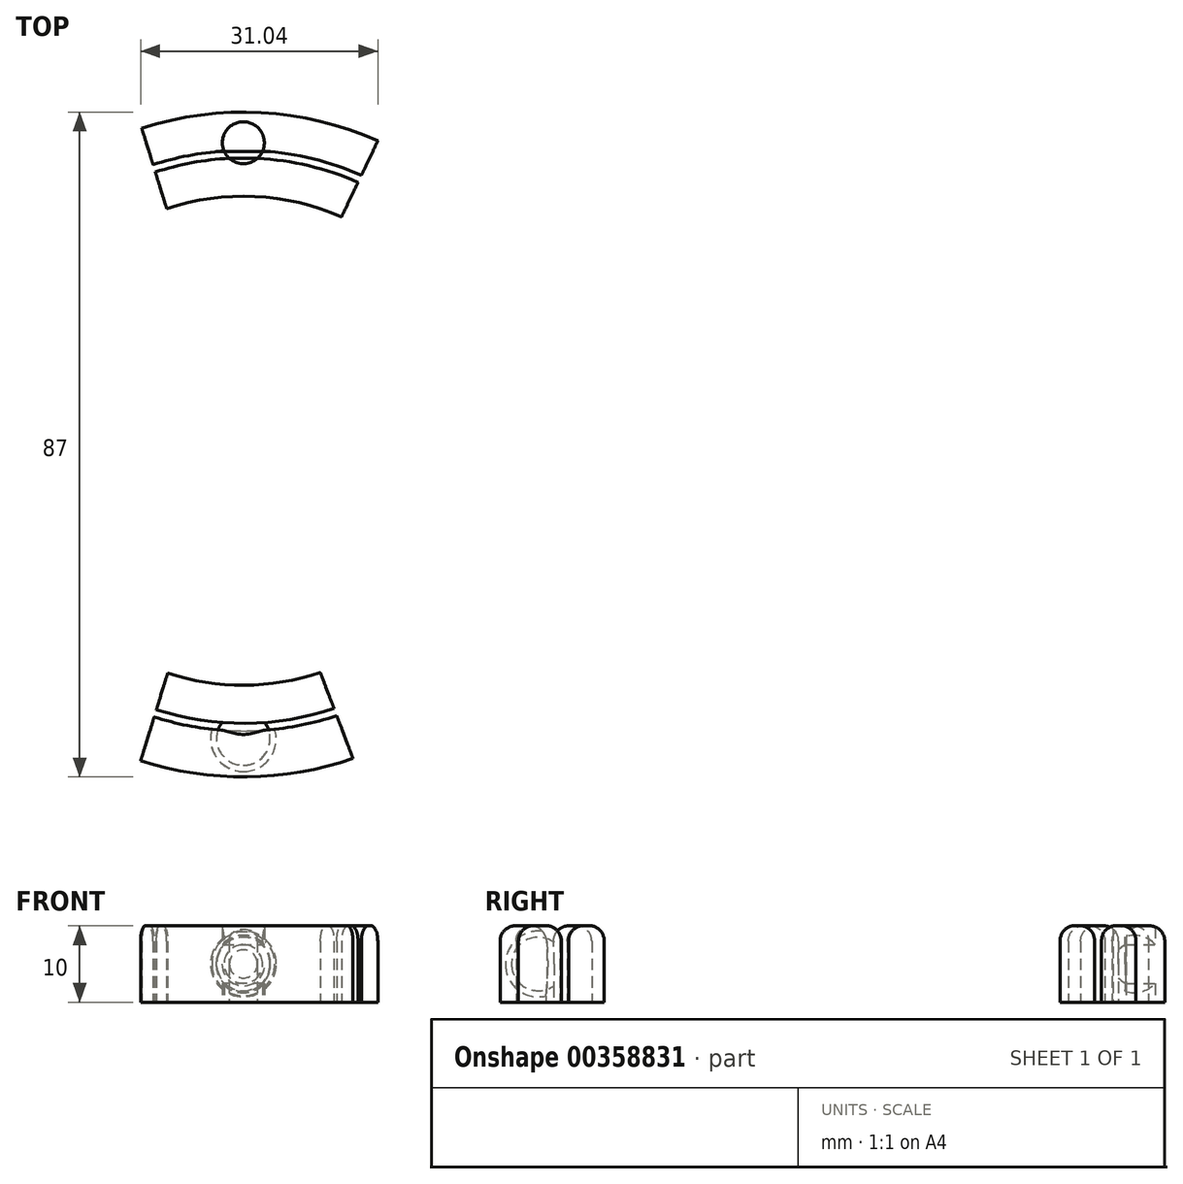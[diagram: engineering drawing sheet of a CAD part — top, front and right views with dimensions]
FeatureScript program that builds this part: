
annotation { "Feature Type Name" : "Feature", "Feature Type Description" : "" }
export const myFeature = defineFeature(function(context is Context, id is Id, definition is map)
    precondition{}
    {
        {
            var Q0;
            Q0=qCreatedBy(makeId("Top.planeOp"),FACE);
            var sketch = newSketch(context, id + "F0", { "sketchPlane" : qUnion([Q0])});
            skArc(sketch, "E0", {"start": v(12.86, 29.3) * mm, "mid": v(1.51, 31.96) * mm, "end": v(-10.03, 30.39) * mm});
            skArc(sketch, "E1.0", {"start": v(15.01, 33.82) * mm, "mid": v(8.57, 36) * mm, "end": v(1.84, 36.95) * mm});
            skArc(sketch, "E2.0", {"start": v(15.44, 34.72) * mm, "mid": v(9.13, 36.89) * mm, "end": v(2.53, 37.92) * mm});
            skArc(sketch, "E3.0", {"start": v(17.6, 39.23) * mm, "mid": v(2.3, 42.94) * mm, "end": v(-13.3, 40.9) * mm});
            skLineSegment(sketch, "E4", {"start": v(-13.3, 40.9) * mm, "end": v(-10.03, 30.39) * mm});
            skLineSegment(sketch, "E5", {"start": v(12.86, 29.3) * mm, "end": v(17.6, 39.23) * mm});
            skCircle(sketch, "E6", {"center": v(0, 39) * mm, "radius": 2.75 * mm});
            skArc(sketch, "E7.0", {"start": v(3.56, 37.83) * mm, "mid": v(0, 42.75) * mm, "end": v(-3.56, 37.83) * mm});
            skArc(sketch, "E8.trimOffspring", {"start": v(-1.84, 36.95) * mm, "mid": v(-6.74, 36.38) * mm, "end": v(-11.52, 35.16) * mm});
            skArc(sketch, "E9.trimOffspring", {"start": v(-2.53, 37.92) * mm, "mid": v(-7.23, 37.3) * mm, "end": v(-11.81, 36.12) * mm});
            skLineSegment(sketch, "E10", {"start": v(0, 43.86) * mm, "end": v(0, 33.98) * mm});
            skLineSegment(sketch, "E11", {"start": v(-1.84, 36.95) * mm, "end": v(1.84, 36.95) * mm});
            skLineSegment(sketch, "E12", {"start": v(-2.53, 37.92) * mm, "end": v(2.53, 37.92) * mm});
            skSolve(sketch);
        }
        {
            var Q0;
            {var subQ3=sQuery(id+"F0.wireOp",EDGE,"E4");var subQ7=sQuery(id+"F0.wireOp",EDGE,"E3.0");var subQ8=makeQuery(id+"F0.imprint","INTERSECT",VERTEX,{"derivedFrom":[subQ7,subQ3]});Q0=makeQuery(id+"F0.imprint","IMPRINT",FACE,{"disambiguationData":[TD([[makeQuery(id+"F0.imprint","IMPRINT",EDGE,{"disambiguationData":[TD([[subQ8,1.0]])],"derivedFrom":subQ7}),1.0]])]});}
            var Q1;
            {var subQ1=sQuery(id+"F0.wireOp",EDGE,"E2.0");var subQ5=sQuery(id+"F0.wireOp",EDGE,"E5");var subQ6=makeQuery(id+"F0.imprint","INTERSECT",VERTEX,{"derivedFrom":[subQ1,subQ5]});Q1=makeQuery(id+"F0.imprint","IMPRINT",FACE,{"disambiguationData":[TD([[makeQuery(id+"F0.imprint","IMPRINT",EDGE,{"disambiguationData":[TD([[subQ6,-1.0]])],"derivedFrom":subQ1}),-1.0]])]});}
            var Q2;
            {var subQ1=sQuery(id+"F0.wireOp",EDGE,"E6");var subQ3=sQuery(id+"F0.wireOp",EDGE,"E10");var subQ4=makeQuery(id+"F0.imprint","INTERSECT",VERTEX,{"disambiguationData":[OD(1.0)],"derivedFrom":[subQ1,subQ3]});Q2=makeQuery(id+"F0.imprint","IMPRINT",FACE,{"disambiguationData":[TD([[makeQuery(id+"F0.imprint","IMPRINT",EDGE,{"disambiguationData":[TD([[subQ4,-1.0]])],"derivedFrom":subQ3}),1.0]])]});}
            var Q3;
            {var subQ1=sQuery(id+"F0.wireOp",EDGE,"E6");var subQ3=sQuery(id+"F0.wireOp",EDGE,"E10");var subQ4=makeQuery(id+"F0.imprint","INTERSECT",VERTEX,{"disambiguationData":[OD(1.0)],"derivedFrom":[subQ1,subQ3]});Q3=makeQuery(id+"F0.imprint","IMPRINT",FACE,{"disambiguationData":[TD([[makeQuery(id+"F0.imprint","IMPRINT",EDGE,{"disambiguationData":[TD([[subQ4,-1.0]])],"derivedFrom":subQ3}),-1.0]])]});}
            var Q4;
            {var subQ0=sQuery(id+"F0.wireOp",EDGE,"E9.trimOffspring");var subQ5=sQuery(id+"F0.wireOp",EDGE,"E7.0");var subQ6=makeQuery(id+"F0.imprint","INTERSECT",VERTEX,{"derivedFrom":[subQ5,subQ0]});Q4=makeQuery(id+"F0.imprint","IMPRINT",FACE,{"disambiguationData":[TD([[makeQuery(id+"F0.imprint","IMPRINT",EDGE,{"disambiguationData":[TD([[subQ6,1.0]])],"derivedFrom":subQ5}),1.0]])]});}
            var Q5;
            {var subQ1=sQuery(id+"F0.wireOp",EDGE,"E2.0");var subQ3=sQuery(id+"F0.wireOp",EDGE,"E7.0");var subQ4=makeQuery(id+"F0.imprint","INTERSECT",VERTEX,{"derivedFrom":[subQ1,subQ3]});Q5=makeQuery(id+"F0.imprint","IMPRINT",FACE,{"disambiguationData":[TD([[makeQuery(id+"F0.imprint","IMPRINT",EDGE,{"disambiguationData":[TD([[subQ4,-1.0]])],"derivedFrom":subQ3}),1.0]])]});}
            extrude(context, id + "F1", {"entities" : qUnion([Q0, Q1, Q2, Q3, Q4, Q5]), "endBound" : BoundingType.SYMMETRIC, "depth" : 10 * mm});
        }
        {
            var Q0;
            Q0=qCreatedBy(makeId("Top.planeOp"),FACE);
            var sketch = newSketch(context, id + "F2", { "sketchPlane" : qUnion([Q0])});
            skArc(sketch, "E13", {"start": v(-9.9, -30.43) * mm, "mid": v(0.1, -32) * mm, "end": v(10.09, -30.37) * mm});
            skArc(sketch, "E14.0", {"start": v(-11.38, -35.2) * mm, "mid": v(0.26, -37) * mm, "end": v(11.87, -35.05) * mm});
            skArc(sketch, "E15.0", {"start": v(-11.67, -36.16) * mm, "mid": v(0.29, -38) * mm, "end": v(12.22, -35.98) * mm});
            skArc(sketch, "E16.0", {"start": v(-13.44, -41.9) * mm, "mid": v(0.48, -44) * mm, "end": v(14.35, -41.6) * mm});
            skCircle(sketch, "E17", {"center": v(0, -39) * mm, "radius": 3.5 * mm});
            skArc(sketch, "E18.0", {"start": v(-4.12, -37.78) * mm, "mid": v(0, -43.3) * mm, "end": v(4.12, -37.78) * mm});
            skLineSegment(sketch, "E19", {"start": v(-9.9, -30.43) * mm, "end": v(-13.44, -41.9) * mm});
            skLineSegment(sketch, "E20", {"start": v(10.09, -30.37) * mm, "end": v(14.35, -41.6) * mm});
            skLineSegment(sketch, "E21", {"start": v(0, -33.12) * mm, "end": v(0, -46.67) * mm});
            skSolve(sketch);
        }
        {
            var Q0;
            {var subQ1=sQuery(id+"F0.wireOp",EDGE,"E0");Q0=makeQuery(id+"F0.imprint","IMPRINT",FACE,{"disambiguationData":[TD([[makeQuery(id+"F0.imprint","IMPRINT",EDGE,{"derivedFrom":subQ1}),-1.0]])]});}
            var Q1;
            {var subQ1=sQuery(id+"F0.wireOp",EDGE,"E6");var subQ3=sQuery(id+"F0.wireOp",EDGE,"E10");var subQ4=makeQuery(id+"F0.imprint","INTERSECT",VERTEX,{"disambiguationData":[OD(0.0)],"derivedFrom":[subQ1,subQ3]});Q1=makeQuery(id+"F0.imprint","IMPRINT",FACE,{"disambiguationData":[TD([[makeQuery(id+"F0.imprint","IMPRINT",EDGE,{"disambiguationData":[TD([[subQ4,1.0]])],"derivedFrom":subQ3}),-1.0]])]});}
            var Q2;
            {var subQ1=sQuery(id+"F0.wireOp",EDGE,"E6");var subQ3=sQuery(id+"F0.wireOp",EDGE,"E10");var subQ4=makeQuery(id+"F0.imprint","INTERSECT",VERTEX,{"disambiguationData":[OD(0.0)],"derivedFrom":[subQ1,subQ3]});Q2=makeQuery(id+"F0.imprint","IMPRINT",FACE,{"disambiguationData":[TD([[makeQuery(id+"F0.imprint","IMPRINT",EDGE,{"disambiguationData":[TD([[subQ4,1.0]])],"derivedFrom":subQ3}),1.0]])]});}
            extrude(context, id + "F3", {"entities" : qUnion([Q0, Q1, Q2]), "endBound" : BoundingType.SYMMETRIC, "depth" : 10 * mm});
        }
        {
            var Q0;
            {var subQ0=sQuery(id+"F0.wireOp",EDGE,"E6");var subQ1=makeQuery(id+"F0.imprint","INTERSECT",VERTEX,{"derivedFrom":[subQ0,sQuery(id+"F0.wireOp",EDGE,"E9.trimOffspring")]});Q0=makeQuery(id+"F0.imprint","IMPRINT",FACE,{"disambiguationData":[TD([[makeQuery(id+"F0.imprint","IMPRINT",EDGE,{"disambiguationData":[TD([[subQ1,1.0]])],"derivedFrom":subQ0}),1.0]])]});}
            var Q1;
            Q1=sQuery(id+"F0.wireOp",EDGE,"E10");
            revolve(context, id + "F4", {"entities" : qUnion([Q0]), "axis" : qUnion([Q1]), "revolveType" : RevolveType.FULL});
        }
        {
            var Q0;
            {var subQ1=sQuery(id+"F0.wireOp",EDGE,"E6");var subQ3=sQuery(id+"F0.wireOp",EDGE,"E10");var subQ4=makeQuery(id+"F0.imprint","INTERSECT",VERTEX,{"disambiguationData":[OD(0.0)],"derivedFrom":[subQ1,subQ3]});Q0=makeQuery(id+"F0.imprint","IMPRINT",FACE,{"disambiguationData":[TD([[makeQuery(id+"F0.imprint","IMPRINT",EDGE,{"disambiguationData":[TD([[subQ4,1.0]])],"derivedFrom":subQ3}),-1.0]])]});}
            var Q1;
            Q1=sQuery(id+"F0.wireOp",EDGE,"E10");
            revolve(context, id + "F5", {"operationType" : NewBodyOperationType.ADD, "entities" : qUnion([Q0]), "axis" : qUnion([Q1]), "revolveType" : RevolveType.FULL});
        }
        {
            var Q0;
            {var subQ0=sQuery(id+"F0.wireOp",EDGE,"E9.trimOffspring");var subQ5=sQuery(id+"F0.wireOp",EDGE,"E7.0");var subQ6=makeQuery(id+"F0.imprint","INTERSECT",VERTEX,{"derivedFrom":[subQ5,subQ0]});Q0=makeQuery(id+"F0.imprint","IMPRINT",FACE,{"disambiguationData":[TD([[makeQuery(id+"F0.imprint","IMPRINT",EDGE,{"disambiguationData":[TD([[subQ6,1.0]])],"derivedFrom":subQ5}),1.0]])]});}
            var Q1;
            Q1=sQuery(id+"F0.wireOp",EDGE,"E10");
            revolve(context, id + "F6", {"operationType" : NewBodyOperationType.REMOVE, "entities" : qUnion([Q0]), "axis" : qUnion([Q1]), "revolveType" : RevolveType.FULL});
        }
        {
            var Q0;
            {var subQ3=sQuery(id+"F0.wireOp",EDGE,"E12");var subQ5=sQuery(id+"F0.wireOp",EDGE,"E10");var subQ7=makeQuery(id+"F0.imprint","INTERSECT",VERTEX,{"derivedFrom":[subQ5,subQ3]});Q0=makeQuery(id+"F0.imprint","IMPRINT",FACE,{"disambiguationData":[TD([[makeQuery(id+"F0.imprint","IMPRINT",EDGE,{"disambiguationData":[TD([[subQ7,-1.0]])],"derivedFrom":subQ5}),-1.0]])]});}
            var Q1;
            Q1=sQuery(id+"F0.wireOp",EDGE,"E10");
            revolve(context, id + "F7", {"operationType" : NewBodyOperationType.ADD, "entities" : qUnion([Q0]), "axis" : qUnion([Q1]), "revolveType" : RevolveType.FULL});
        }
        {
            var Q0;
            {var subQ1=sQuery(id+"F0.wireOp",EDGE,"E6");var subQ3=sQuery(id+"F0.wireOp",EDGE,"E10");var subQ4=makeQuery(id+"F0.imprint","INTERSECT",VERTEX,{"disambiguationData":[OD(0.0)],"derivedFrom":[subQ1,subQ3]});Q0=makeQuery(id+"F0.imprint","IMPRINT",FACE,{"disambiguationData":[TD([[makeQuery(id+"F0.imprint","IMPRINT",EDGE,{"disambiguationData":[TD([[subQ4,1.0]])],"derivedFrom":subQ3}),-1.0]])]});}
            var Q1;
            Q1=sQuery(id+"F0.wireOp",EDGE,"E10");
            revolve(context, id + "F8", {"operationType" : NewBodyOperationType.ADD, "entities" : qUnion([Q0]), "axis" : qUnion([Q1]), "revolveType" : RevolveType.FULL});
        }
        {
            var Q0;
            Q0=makeQuery(id+"F1.opExtrude","CAP_EDGE",EDGE,{"disambiguationData":[OSD([sQuery(id+"F0.wireOp",EDGE,"E3.0")])],"isStart":false});
            var Q1;
            Q1=makeQuery(id+"F1.opExtrude","CAP_EDGE",EDGE,{"disambiguationData":[OSD([sQuery(id+"F0.wireOp",EDGE,"E9.trimOffspring")])],"isStart":false});
            var Q2;
            Q2=makeQuery(id+"F1.opExtrude","CAP_EDGE",EDGE,{"disambiguationData":[OSD([sQuery(id+"F0.wireOp",EDGE,"E12")])],"isStart":false});
            var Q3;
            Q3=makeQuery(id+"F1.opExtrude","CAP_EDGE",EDGE,{"disambiguationData":[OSD([sQuery(id+"F0.wireOp",EDGE,"E2.0")])],"isStart":false});
            var Q4;
            Q4=makeQuery(id+"F3.opExtrude","CAP_EDGE",EDGE,{"disambiguationData":[OSD([sQuery(id+"F0.wireOp",EDGE,"E11")])],"isStart":false});
            var Q5;
            Q5=makeQuery(id+"F3.opExtrude","CAP_EDGE",EDGE,{"disambiguationData":[OSD([sQuery(id+"F0.wireOp",EDGE,"E8.trimOffspring")])],"isStart":false});
            var Q6;
            Q6=makeQuery(id+"F3.opExtrude","CAP_EDGE",EDGE,{"disambiguationData":[OSD([sQuery(id+"F0.wireOp",EDGE,"E1.0")])],"isStart":false});
            var Q7;
            Q7=makeQuery(id+"F3.opExtrude","CAP_EDGE",EDGE,{"disambiguationData":[OSD([sQuery(id+"F0.wireOp",EDGE,"E0")])],"isStart":false});
            fillet(context, id + "F9", {"entities" : qUnion([Q0, Q1, Q2, Q3, Q4, Q5, Q6, Q7]), "radius" : 2 * mm, "tangentPropagation" : true, "allowEdgeOverflow" : false});
        }
        {
            var Q0;
            {var subQ0=sQuery(id+"F2.wireOp",EDGE,"E17");var subQ1=sQuery(id+"F2.wireOp",EDGE,"E14.0");var subQ2=makeQuery(id+"F2.imprint","INTERSECT",VERTEX,{"disambiguationData":[OD(0.0)],"derivedFrom":[subQ1,subQ0]});Q0=makeQuery(id+"F2.imprint","IMPRINT",FACE,{"disambiguationData":[TD([[makeQuery(id+"F2.imprint","IMPRINT",EDGE,{"disambiguationData":[TD([[subQ2,-1.0]])],"derivedFrom":subQ1}),1.0]])]});}
            var Q1;
            {var subQ0=sQuery(id+"F2.wireOp",EDGE,"E17");var subQ1=sQuery(id+"F2.wireOp",EDGE,"E14.0");var subQ2=makeQuery(id+"F2.imprint","INTERSECT",VERTEX,{"disambiguationData":[OD(0.0)],"derivedFrom":[subQ1,subQ0]});Q1=makeQuery(id+"F2.imprint","IMPRINT",FACE,{"disambiguationData":[TD([[makeQuery(id+"F2.imprint","IMPRINT",EDGE,{"disambiguationData":[TD([[subQ2,-1.0]])],"derivedFrom":subQ1}),-1.0]])]});}
            var Q2;
            {var subQ0=sQuery(id+"F2.wireOp",EDGE,"E17");var subQ1=sQuery(id+"F2.wireOp",EDGE,"E15.0");var subQ2=makeQuery(id+"F2.imprint","INTERSECT",VERTEX,{"disambiguationData":[OD(0.0)],"derivedFrom":[subQ1,subQ0]});Q2=makeQuery(id+"F2.imprint","IMPRINT",FACE,{"disambiguationData":[TD([[makeQuery(id+"F2.imprint","IMPRINT",EDGE,{"disambiguationData":[TD([[subQ2,-1.0]])],"derivedFrom":subQ1}),-1.0]])]});}
            var Q3;
            Q3=sQuery(id+"F2.wireOp",EDGE,"E21");
            revolve(context, id + "F10", {"operationType" : NewBodyOperationType.ADD, "entities" : qUnion([Q0, Q1, Q2]), "axis" : qUnion([Q3]), "revolveType" : RevolveType.FULL});
        }
        {
            var Q0;
            {var subQ0=sQuery(id+"F2.wireOp",EDGE,"E18.0");var subQ1=sQuery(id+"F2.wireOp",EDGE,"E15.0");var subQ2=makeQuery(id+"F2.imprint","INTERSECT",VERTEX,{"disambiguationData":[OD(0.0)],"derivedFrom":[subQ1,subQ0]});Q0=makeQuery(id+"F2.imprint","IMPRINT",FACE,{"disambiguationData":[TD([[makeQuery(id+"F2.imprint","IMPRINT",EDGE,{"disambiguationData":[TD([[subQ2,-1.0]])],"derivedFrom":subQ1}),-1.0]])]});}
            var Q1;
            Q1=sQuery(id+"F2.wireOp",EDGE,"E21");
            revolve(context, id + "F11", {"operationType" : NewBodyOperationType.REMOVE, "entities" : qUnion([Q0]), "axis" : qUnion([Q1]), "revolveType" : RevolveType.FULL, "oppositeDirection" : true});
        }
        {
            var Q0;
            {var subQ0=sQuery(id+"F2.wireOp",EDGE,"E17");var subQ1=sQuery(id+"F2.wireOp",EDGE,"E14.0");var subQ2=makeQuery(id+"F2.imprint","INTERSECT",VERTEX,{"disambiguationData":[OD(0.0)],"derivedFrom":[subQ1,subQ0]});Q0=makeQuery(id+"F2.imprint","IMPRINT",FACE,{"disambiguationData":[TD([[makeQuery(id+"F2.imprint","IMPRINT",EDGE,{"disambiguationData":[TD([[subQ2,-1.0]])],"derivedFrom":subQ1}),1.0]])]});}
            var Q1;
            {var subQ0=sQuery(id+"F2.wireOp",EDGE,"E21");var subQ1=sQuery(id+"F2.wireOp",EDGE,"E14.0");var subQ2=makeQuery(id+"F2.imprint","INTERSECT",VERTEX,{"derivedFrom":[subQ1,subQ0]});Q1=makeQuery(id+"F2.imprint","IMPRINT",FACE,{"disambiguationData":[TD([[makeQuery(id+"F2.imprint","IMPRINT",EDGE,{"disambiguationData":[TD([[subQ2,-1.0]])],"derivedFrom":subQ1}),1.0]])]});}
            var Q2;
            {var subQ9=sQuery(id+"F2.wireOp",EDGE,"E13");Q2=makeQuery(id+"F2.imprint","IMPRINT",FACE,{"disambiguationData":[TD([[makeQuery(id+"F2.imprint","IMPRINT",EDGE,{"derivedFrom":subQ9}),-1.0]])]});}
            var Q3;
            {var subQ0=sQuery(id+"F2.wireOp",EDGE,"E17");var subQ1=sQuery(id+"F2.wireOp",EDGE,"E15.0");var subQ2=makeQuery(id+"F2.imprint","INTERSECT",VERTEX,{"disambiguationData":[OD(0.0)],"derivedFrom":[subQ1,subQ0]});Q3=makeQuery(id+"F2.imprint","IMPRINT",FACE,{"disambiguationData":[TD([[makeQuery(id+"F2.imprint","IMPRINT",EDGE,{"disambiguationData":[TD([[subQ2,-1.0]])],"derivedFrom":subQ1}),-1.0]])]});}
            var Q4;
            {var subQ0=sQuery(id+"F2.wireOp",EDGE,"E18.0");var subQ1=sQuery(id+"F2.wireOp",EDGE,"E15.0");var subQ2=makeQuery(id+"F2.imprint","INTERSECT",VERTEX,{"disambiguationData":[OD(0.0)],"derivedFrom":[subQ1,subQ0]});Q4=makeQuery(id+"F2.imprint","IMPRINT",FACE,{"disambiguationData":[TD([[makeQuery(id+"F2.imprint","IMPRINT",EDGE,{"disambiguationData":[TD([[subQ2,-1.0]])],"derivedFrom":subQ1}),-1.0]])]});}
            var Q5;
            {var subQ0=sQuery(id+"F2.wireOp",EDGE,"E19");var subQ1=sQuery(id+"F2.wireOp",EDGE,"E15.0");var subQ2=makeQuery(id+"F2.imprint","INTERSECT",VERTEX,{"derivedFrom":[subQ1,subQ0]});Q5=makeQuery(id+"F2.imprint","IMPRINT",FACE,{"disambiguationData":[TD([[makeQuery(id+"F2.imprint","IMPRINT",EDGE,{"disambiguationData":[TD([[subQ2,-1.0]])],"derivedFrom":subQ1}),-1.0]])]});}
            var Q6;
            {var subQ0=sQuery(id+"F2.wireOp",EDGE,"E18.0");var subQ1=sQuery(id+"F2.wireOp",EDGE,"E15.0");var subQ2=makeQuery(id+"F2.imprint","INTERSECT",VERTEX,{"disambiguationData":[OD(1.0)],"derivedFrom":[subQ1,subQ0]});Q6=makeQuery(id+"F2.imprint","IMPRINT",FACE,{"disambiguationData":[TD([[makeQuery(id+"F2.imprint","IMPRINT",EDGE,{"disambiguationData":[TD([[subQ2,1.0]])],"derivedFrom":subQ1}),-1.0]])]});}
            var Q7;
            {var subQ0=sQuery(id+"F2.wireOp",EDGE,"E20");var subQ1=sQuery(id+"F2.wireOp",EDGE,"E15.0");var subQ2=makeQuery(id+"F2.imprint","INTERSECT",VERTEX,{"derivedFrom":[subQ1,subQ0]});Q7=makeQuery(id+"F2.imprint","IMPRINT",FACE,{"disambiguationData":[TD([[makeQuery(id+"F2.imprint","IMPRINT",EDGE,{"disambiguationData":[TD([[subQ2,1.0]])],"derivedFrom":subQ1}),-1.0]])]});}
            var Q8;
            {var subQ0=sQuery(id+"F2.wireOp",EDGE,"E21");var subQ1=sQuery(id+"F2.wireOp",EDGE,"E15.0");var subQ2=makeQuery(id+"F2.imprint","INTERSECT",VERTEX,{"derivedFrom":[subQ1,subQ0]});Q8=makeQuery(id+"F2.imprint","IMPRINT",FACE,{"disambiguationData":[TD([[makeQuery(id+"F2.imprint","IMPRINT",EDGE,{"disambiguationData":[TD([[subQ2,-1.0]])],"derivedFrom":subQ1}),-1.0]])]});}
            extrude(context, id + "F12", {"entities" : qUnion([Q0, Q1, Q2, Q3, Q4, Q5, Q6, Q7, Q8]), "operationType" : NewBodyOperationType.ADD, "endBound" : BoundingType.SYMMETRIC, "depth" : 10 * mm});
        }
        {
            var Q0;
            {var subQ0=sQuery(id+"F2.wireOp",EDGE,"E18.0");var subQ1=sQuery(id+"F2.wireOp",EDGE,"E15.0");var subQ2=makeQuery(id+"F2.imprint","INTERSECT",VERTEX,{"disambiguationData":[OD(0.0)],"derivedFrom":[subQ1,subQ0]});Q0=makeQuery(id+"F2.imprint","IMPRINT",FACE,{"disambiguationData":[TD([[makeQuery(id+"F2.imprint","IMPRINT",EDGE,{"disambiguationData":[TD([[subQ2,-1.0]])],"derivedFrom":subQ1}),-1.0]])]});}
            var Q1;
            Q1=sQuery(id+"F2.wireOp",EDGE,"E21");
            revolve(context, id + "F13", {"operationType" : NewBodyOperationType.REMOVE, "entities" : qUnion([Q0]), "axis" : qUnion([Q1]), "revolveType" : RevolveType.FULL, "oppositeDirection" : true});
        }
        {
            var Q0;
            Q0=makeQuery(id+"F12.opExtrude","CAP_EDGE",EDGE,{"disambiguationData":[OSD([sQuery(id+"F2.wireOp",EDGE,"E13")])],"isStart":false});
            var Q1;
            Q1=makeQuery(id+"F12.opExtrude","CAP_EDGE",EDGE,{"disambiguationData":[OSD([sQuery(id+"F2.wireOp",EDGE,"E14.0")])],"isStart":false});
            var Q2;
            Q2=makeQuery(id+"F12.opExtrude","CAP_EDGE",EDGE,{"disambiguationData":[OSD([sQuery(id+"F2.wireOp",EDGE,"E15.0")])],"isStart":false});
            var Q3;
            Q3=makeQuery(id+"F12.opExtrude","CAP_EDGE",EDGE,{"disambiguationData":[OSD([sQuery(id+"F2.wireOp",EDGE,"E16.0")])],"isStart":false});
            fillet(context, id + "F14", {"entities" : qUnion([Q0, Q1, Q2, Q3]), "radius" : 2 * mm, "tangentPropagation" : true, "allowEdgeOverflow" : false});
        }
    });
